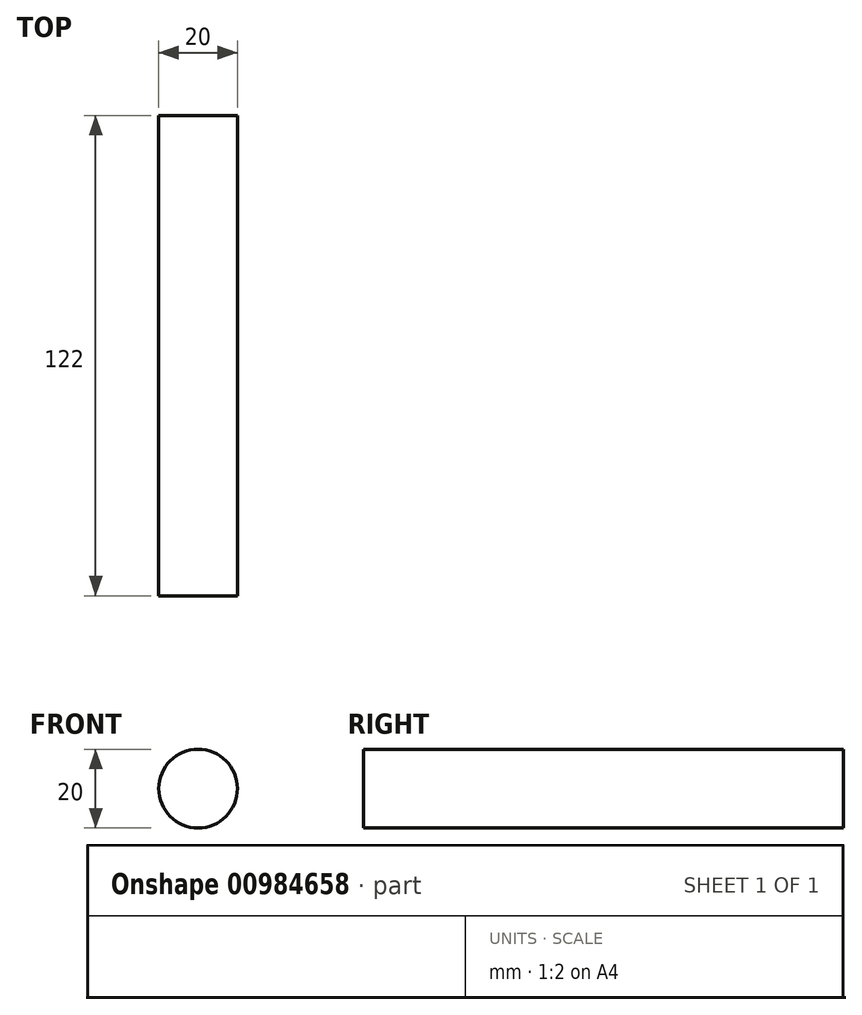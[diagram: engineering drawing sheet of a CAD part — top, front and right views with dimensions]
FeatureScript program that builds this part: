
annotation { "Feature Type Name" : "Feature", "Feature Type Description" : "" }
export const myFeature = defineFeature(function(context is Context, id is Id, definition is map)
    precondition{}
    {
        {
            var Q0;
            Q0=qCreatedBy(makeId("Front.planeOp"),FACE);
            var sketch = newSketch(context, id + "F0", { "sketchPlane" : qUnion([Q0])});
            skCircle(sketch, "E0", {"center": v(0, 0) * mm, "radius": 10 * mm});
            skSolve(sketch);
        }
        {
            var Q0;
            Q0 = qSketchRegion(id + "F0", true);
            extrude(context, id + "F1", {"entities" : qUnion([Q0]), "depth" : 122 * mm, "offsetDistance" : 25 * mm});
        }
    });
